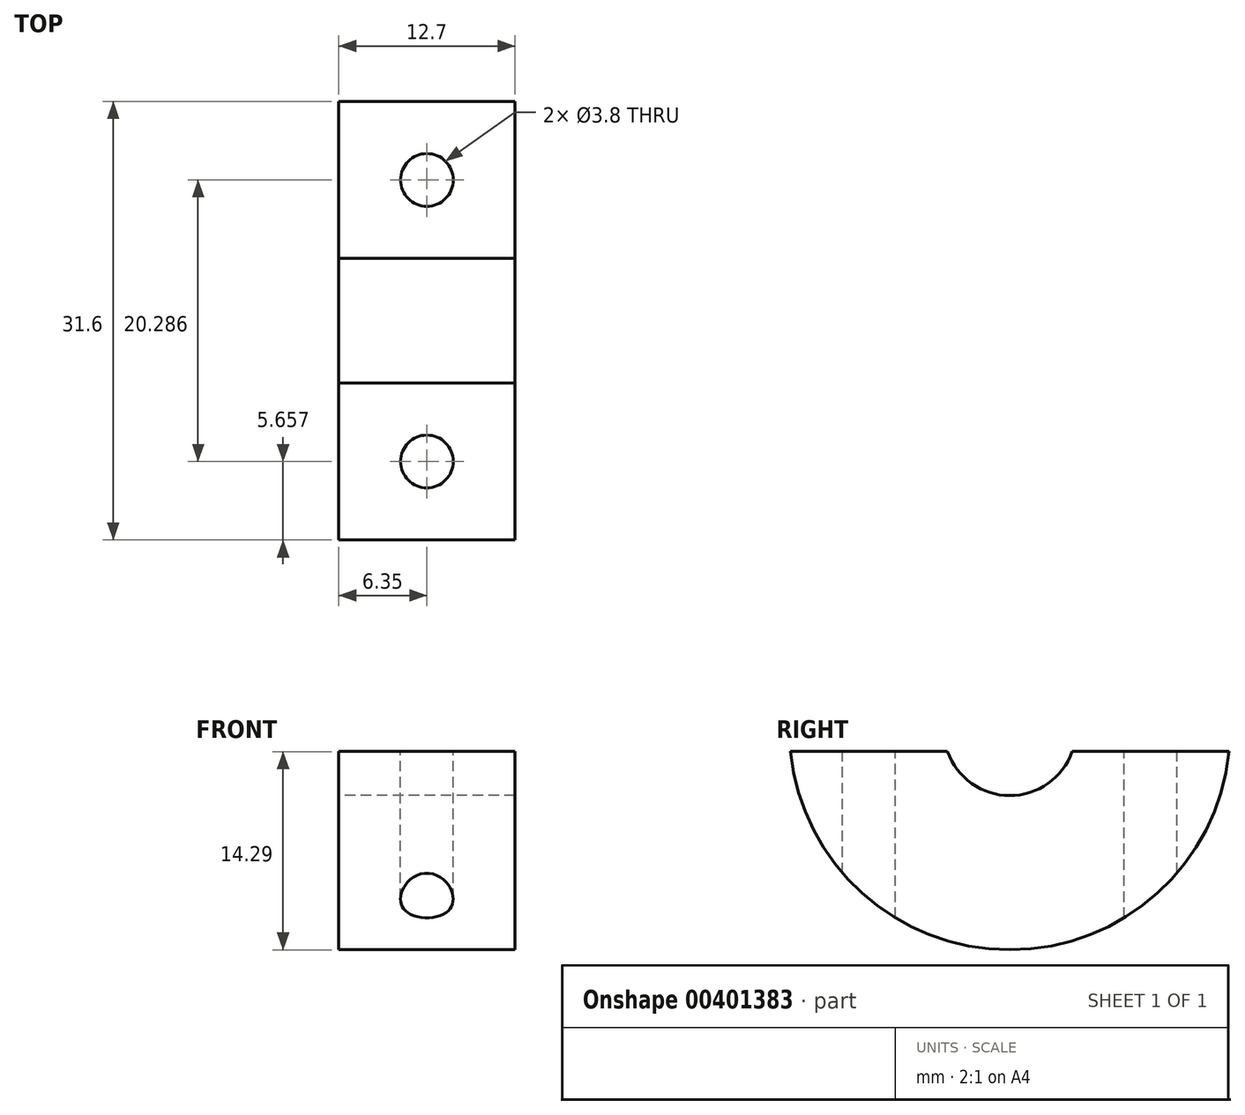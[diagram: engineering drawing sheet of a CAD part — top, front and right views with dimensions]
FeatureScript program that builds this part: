
annotation { "Feature Type Name" : "Feature", "Feature Type Description" : "" }
export const myFeature = defineFeature(function(context is Context, id is Id, definition is map)
    precondition{}
    {
        {
            var Q0;
            Q0=qCreatedBy(makeId("Right.planeOp"),FACE);
            var sketch = newSketch(context, id + "F0", { "sketchPlane" : qUnion([Q0])});
            skCircle(sketch, "E0", {"center": v(0, 0) * mm, "radius": 15.88 * mm});
            skCircle(sketch, "E1", {"center": v(0, 0) * mm, "radius": 4.76 * mm});
            skSolve(sketch);
        }
        {
            var Q0;
            Q0 = qSketchRegion(id + "F0", true);
            extrude(context, id + "F1", {"entities" : qUnion([Q0]), "depth" : 12.7 * mm});
        }
        {
            var Q0;
            Q0=makeQuery(id+"F1.opExtrude","CAP_FACE",FACE,{"disambiguationData":[OSD([sQuery(id+"F0.wireOp",EDGE,"E0"),sQuery(id+"F0.wireOp",EDGE,"E1")])],"isStart":false});
            var sketch = newSketch(context, id + "F2", { "sketchPlane" : qUnion([Q0])});
            skLineSegment(sketch, "E2.bottom", {"start": v(-21.69, -1.59) * mm, "end": v(17.96, -1.59) * mm});
            skLineSegment(sketch, "E2.top", {"start": v(-21.69, 17.85) * mm, "end": v(17.96, 17.85) * mm});
            skLineSegment(sketch, "E2.left", {"start": v(-21.69, -1.59) * mm, "end": v(-21.69, 17.85) * mm});
            skLineSegment(sketch, "E2.right", {"start": v(17.96, -1.59) * mm, "end": v(17.96, 17.85) * mm});
            skSolve(sketch);
        }
        {
            var Q0;
            Q0 = qSketchRegion(id + "F2", true);
            extrude(context, id + "F3", {"entities" : qUnion([Q0]), "operationType" : NewBodyOperationType.REMOVE, "endBound" : BoundingType.THROUGH_ALL, "oppositeDirection" : true, "depth" : 25.4 * mm});
        }
        {
            var Q0;
            Q0=makeQuery(id+"F3.boolean.opBoolean","COPY",FACE,{"disambiguationData":[OD(0.0)],"derivedFrom":makeQuery(id+"F3.opExtrude","SWEPT_FACE",FACE,{"disambiguationData":[OSD([sQuery(id+"F2.wireOp",EDGE,"E2.bottom")])]})});
            var sketch = newSketch(context, id + "F4", { "sketchPlane" : qUnion([Q0])});
            skCircle(sketch, "E3", {"center": v(6.35, -10.14) * mm, "radius": 1.9 * mm});
            skLineSegment(sketch, "E4", {"start": v(6.35, -10.14) * mm, "end": v(6.35, -15.8) * mm, "construction": true});
            skLineSegment(sketch, "E5", {"start": v(6.35, -15.8) * mm, "end": v(6.35, -10.14) * mm, "construction": true});
            skLineSegment(sketch, "E6", {"start": v(6.35, -4.5) * mm, "end": v(6.35, -10.14) * mm, "construction": true});
            skCircle(sketch, "E7.MirrorC", {"center": v(6.35, 10.14) * mm, "radius": 1.9 * mm});
            skSolve(sketch);
        }
        {
            var Q0;
            Q0 = qSketchRegion(id + "F4", true);
            extrude(context, id + "F5", {"entities" : qUnion([Q0]), "operationType" : NewBodyOperationType.REMOVE, "endBound" : BoundingType.THROUGH_ALL, "oppositeDirection" : true, "depth" : 25.4 * mm});
        }
        {
            var Q0;
            Q0=qCreatedBy(makeId("Top.planeOp"),FACE);
            cPlane(context, id + "F6", {"entities" : qUnion([Q0]), "cplaneType" : CPlaneType.OFFSET, "offset" : 15.88 * mm, "oppositeDirection" : true, "width" : 152.4 * mm, "height" : 152.4 * mm});
        }
        {
            var Q0;
            Q0=qCreatedBy(id+"F6.planeOp",FACE);
            var sketch = newSketch(context, id + "F7", { "sketchPlane" : qUnion([Q0])});
            skCircle(sketch, "E8", {"center": v(6.35, 10.14) * mm, "radius": 4.76 * mm});
            skCircle(sketch, "E9.MirrorC", {"center": v(6.35, -10.14) * mm, "radius": 4.76 * mm});
            skSolve(sketch);
        }
        {
            var Q0;
            Q0 = qSketchRegion(id + "F7", true);
            extrude(context, id + "F8", {"entities" : qUnion([Q0]), "operationType" : NewBodyOperationType.REMOVE, "depth" : 3 / 203.2 * mm});
        }
    });
